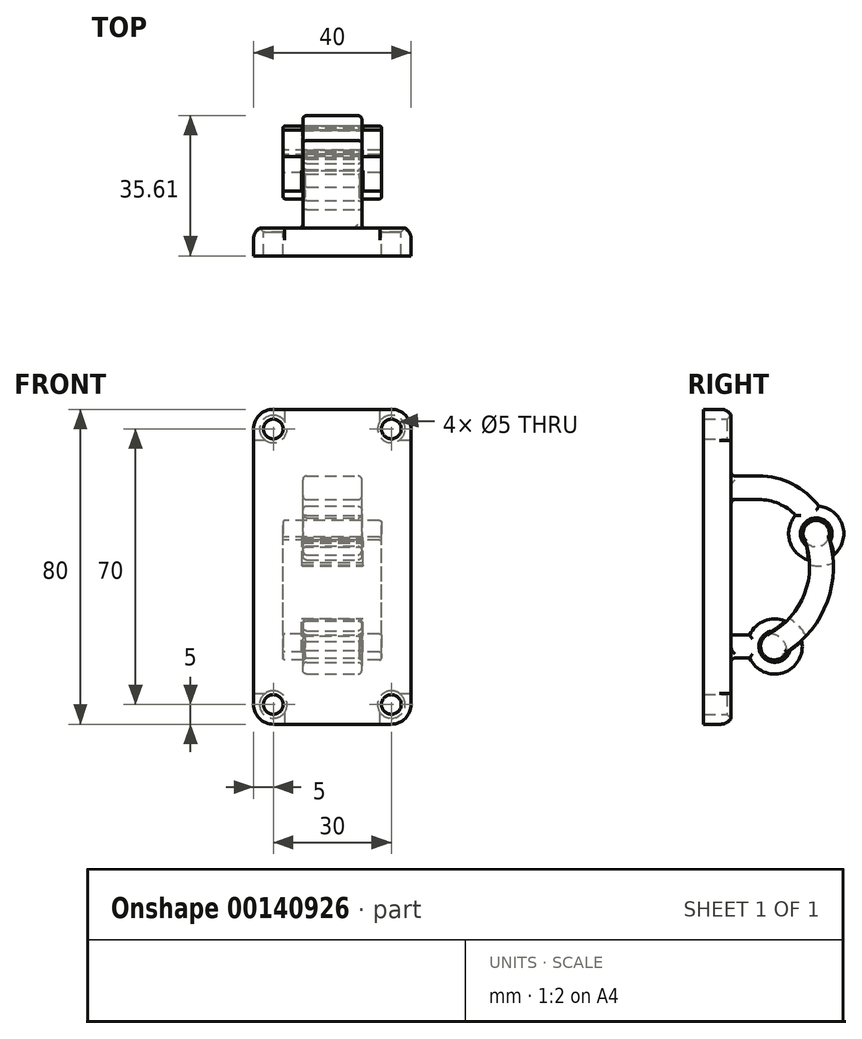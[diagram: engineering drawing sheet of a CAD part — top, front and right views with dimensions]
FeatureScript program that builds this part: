
annotation { "Feature Type Name" : "Feature", "Feature Type Description" : "" }
export const myFeature = defineFeature(function(context is Context, id is Id, definition is map)
    precondition{}
    {
        {
            var Q0;
            Q0=qCreatedBy(makeId("Front.planeOp"),FACE);
            var sketch = newSketch(context, id + "F0", { "sketchPlane" : qUnion([Q0])});
            skLineSegment(sketch, "E0.bottom", {"start": v(-15, 40) * mm, "end": v(15, 40) * mm});
            skLineSegment(sketch, "E0.top", {"start": v(-15, -40) * mm, "end": v(15, -40) * mm});
            skLineSegment(sketch, "E0.left", {"start": v(-20, 35) * mm, "end": v(-20, -35) * mm});
            skLineSegment(sketch, "E0.right", {"start": v(20, 35) * mm, "end": v(20, -35) * mm});
            skPoint(sketch, "E0.middle", {"position": v(0, 0) * mm});
            skLineSegment(sketch, "E1.bottom", {"start": v(-7.5, -17) * mm, "end": v(7.5, -17) * mm});
            skLineSegment(sketch, "E1.top", {"start": v(-7.5, -23) * mm, "end": v(7.5, -23) * mm});
            skLineSegment(sketch, "E1.left", {"start": v(-7.5, -17) * mm, "end": v(-7.5, -23) * mm});
            skLineSegment(sketch, "E1.right", {"start": v(7.5, -17) * mm, "end": v(7.5, -23) * mm});
            skPoint(sketch, "E1.middle", {"position": v(0, -20) * mm});
            skLineSegment(sketch, "E2.MirrorCS", {"start": v(-7.5, 17) * mm, "end": v(7.5, 17) * mm});
            skLineSegment(sketch, "E3.MirrorCS", {"start": v(-7.5, 17) * mm, "end": v(-7.5, 23) * mm});
            skLineSegment(sketch, "E4.MirrorCS", {"start": v(-7.5, 23) * mm, "end": v(7.5, 23) * mm});
            skLineSegment(sketch, "E5.MirrorCS", {"start": v(7.5, 17) * mm, "end": v(7.5, 23) * mm});
            skPoint(sketch, "E6.visualSharp", {"position": v(-20, 40) * mm});
            skArc(sketch, "E6.filletArc", {"start": v(-15, 40) * mm, "mid": v(-18.54, 38.54) * mm, "end": v(-20, 35) * mm});
            skPoint(sketch, "E7.visualSharp", {"position": v(20, 40) * mm});
            skArc(sketch, "E7.filletArc", {"start": v(20, 35) * mm, "mid": v(18.54, 38.54) * mm, "end": v(15, 40) * mm});
            skPoint(sketch, "E8.visualSharp", {"position": v(20, -40) * mm});
            skArc(sketch, "E8.filletArc", {"start": v(15, -40) * mm, "mid": v(18.54, -38.54) * mm, "end": v(20, -35) * mm});
            skPoint(sketch, "E9.visualSharp", {"position": v(-20, -40) * mm});
            skArc(sketch, "E9.filletArc", {"start": v(-20, -35) * mm, "mid": v(-18.54, -38.54) * mm, "end": v(-15, -40) * mm});
            skSolve(sketch);
        }
        {
            var Q0;
            Q0=makeQuery(id+"F0.imprint","IMPRINT",FACE,{"disambiguationData":[TD([[makeQuery(id+"F0.imprint","IMPRINT",EDGE,{"derivedFrom":sQuery(id+"F0.wireOp",EDGE,"E2.MirrorCS")}),1.0]])]});
            var Q1;
            Q1=makeQuery(id+"F0.imprint","IMPRINT",FACE,{"disambiguationData":[TD([[makeQuery(id+"F0.imprint","IMPRINT",EDGE,{"derivedFrom":sQuery(id+"F0.wireOp",EDGE,"E0.bottom")}),-1.0]])]});
            var Q2;
            Q2=makeQuery(id+"F0.imprint","IMPRINT",FACE,{"disambiguationData":[TD([[makeQuery(id+"F0.imprint","IMPRINT",EDGE,{"derivedFrom":sQuery(id+"F0.wireOp",EDGE,"E1.bottom")}),-1.0]])]});
            extrude(context, id + "F1", {"entities" : qUnion([Q0, Q1, Q2]), "oppositeDirection" : true, "depth" : 7 * mm});
        }
        {
            var Q0;
            Q0=qCreatedBy(makeId("Right.planeOp"),FACE);
            var sketch = newSketch(context, id + "F2", { "sketchPlane" : qUnion([Q0])});
            skLineSegment(sketch, "E10", {"start": v(-0.47, 23.07) * mm, "end": v(14, 23.07) * mm});
            skLineSegment(sketch, "E11", {"start": v(0, 17.07) * mm, "end": v(14, 17.07) * mm});
            skArc(sketch, "E12", {"start": v(14, 23.07) * mm, "mid": v(24.63, 19.8) * mm, "end": v(31.6, 11.16) * mm});
            skArc(sketch, "E13.0", {"start": v(14, 17.07) * mm, "mid": v(20.84, 15.11) * mm, "end": v(25.63, 9.84) * mm});
            skLineSegment(sketch, "E14", {"start": v(26.97, 4.3) * mm, "end": v(27.77, 4.32) * mm});
            skCircle(sketch, "E15", {"center": v(28.61, 8.4) * mm, "radius": 4 * mm});
            skLineSegment(sketch, "E16", {"start": v(0.13, -17.33) * mm, "end": v(11.71, -17.33) * mm});
            skLineSegment(sketch, "E17", {"start": v(0, -23.2) * mm, "end": v(11.71, -23.2) * mm});
            skArc(sketch, "E18", {"start": v(11.71, -23.2) * mm, "mid": v(25.07, -20.26) * mm, "end": v(11.71, -17.33) * mm});
            skCircle(sketch, "E19", {"center": v(18.07, -20.26) * mm, "radius": 4 * mm});
            skLineSegment(sketch, "E20.trimOffspring", {"start": v(18, -17.33) * mm, "end": v(18.13, -17.33) * mm});
            skLineSegment(sketch, "E21.trimOffspring", {"start": v(32.88, 4.4) * mm, "end": v(32.97, 4.4) * mm});
            skCircle(sketch, "E22.converted", {"center": v(28.61, 8.4) * mm, "radius": 7 * mm});
            skPoint(sketch, "E23.orphan", {"position": v(0, 23.07) * mm});
            skLineSegment(sketch, "E24", {"start": v(0, 23.07) * mm, "end": v(0, 17.07) * mm});
            skLineSegment(sketch, "E25", {"start": v(0.13, -17.33) * mm, "end": v(0, -23.2) * mm});
            skSolve(sketch);
        }
        {
            var Q0;
            Q0=makeQuery(id+"F1.opExtrude","CAP_FACE",FACE,{"disambiguationData":[OSD([sQuery(id+"F0.wireOp",EDGE,"E0.bottom"),sQuery(id+"F0.wireOp",EDGE,"E0.top"),sQuery(id+"F0.wireOp",EDGE,"E0.left"),sQuery(id+"F0.wireOp",EDGE,"E0.right"),sQuery(id+"F0.wireOp",EDGE,"E6.filletArc"),sQuery(id+"F0.wireOp",EDGE,"E7.filletArc"),sQuery(id+"F0.wireOp",EDGE,"E8.filletArc"),sQuery(id+"F0.wireOp",EDGE,"E9.filletArc")])],"isStart":false});
            var sketch = newSketch(context, id + "F3", { "sketchPlane" : qUnion([Q0])});
            skPoint(sketch, "E26", {"position": v(-15, 35) * mm});
            skPoint(sketch, "E27", {"position": v(15, 35) * mm});
            skPoint(sketch, "E28", {"position": v(15, -35) * mm});
            skPoint(sketch, "E29", {"position": v(-15, -35) * mm});
            skSolve(sketch);
        }
        {
            var Q0;
            Q0=sQuery(id+"F3.wireOp",VERTEX,"E27");
            var Q1;
            Q1=sQuery(id+"F3.wireOp",VERTEX,"E26");
            var Q2;
            Q2=sQuery(id+"F3.wireOp",VERTEX,"E28");
            var Q3;
            Q3=sQuery(id+"F3.wireOp",VERTEX,"E29");
            var Q4;
            Q4=makeQuery(id+"F1.opExtrude","SWEPT_BODY",BODY,{"disambiguationData":[OSD([sQuery(id+"F0.wireOp",EDGE,"E0.bottom"),sQuery(id+"F0.wireOp",EDGE,"E0.top"),sQuery(id+"F0.wireOp",EDGE,"E0.left"),sQuery(id+"F0.wireOp",EDGE,"E0.right"),sQuery(id+"F0.wireOp",EDGE,"E6.filletArc"),sQuery(id+"F0.wireOp",EDGE,"E7.filletArc"),sQuery(id+"F0.wireOp",EDGE,"E8.filletArc"),sQuery(id+"F0.wireOp",EDGE,"E9.filletArc")])]});
            hole(context, id + "F4", {"style" : HoleStyle.C_SINK, "endStyle" : HoleEndStyle.THROUGH, "holeDiameter" : 5 * mm, "cSinkDiameter" : 7 * mm, "cSinkAngle" : 90 * degree, "locations" : qUnion([Q0, Q1, Q2, Q3]), "scope" : qUnion([Q4]), "isTappedThrough" : true});
        }
        {
            var Q0;
            Q0=makeQuery(id+"F1.opExtrude","CAP_EDGE",EDGE,{"disambiguationData":[OSD([sQuery(id+"F0.wireOp",EDGE,"E0.bottom")])],"isStart":false});
            fillet(context, id + "F5", {"entities" : qUnion([Q0]), "radius" : 3 * mm, "tangentPropagation" : true, "allowEdgeOverflow" : false});
        }
        {
            var Q0;
            {var subQ1=sQuery(id+"F2.wireOp",EDGE,"E16");Q0=makeQuery(id+"F2.imprint","IMPRINT",FACE,{"disambiguationData":[TD([[makeQuery(id+"F2.imprint","IMPRINT",EDGE,{"derivedFrom":subQ1}),-1.0]])]});}
            var Q1;
            {var subQ0=sQuery(id+"F2.wireOp",EDGE,"C32lH3EJ-jwJ5-gCcF-TI2y-UIbqiRQANIjS");var subQ1=sQuery(id+"F2.wireOp",EDGE,"E18");var subQ2=makeQuery(id+"F2.imprint","INTERSECT",VERTEX,{"derivedFrom":[subQ1,subQ0]});Q1=makeQuery(id+"F2.imprint","IMPRINT",FACE,{"disambiguationData":[TD([[makeQuery(id+"F2.imprint","IMPRINT",EDGE,{"disambiguationData":[TD([[subQ2,-1.0]])],"derivedFrom":subQ1}),1.0]])]});}
            var Q2;
            Q2=makeQuery(id+"F2.imprint","IMPRINT",FACE,{"disambiguationData":[TD([[makeQuery(id+"F2.imprint","IMPRINT",EDGE,{"derivedFrom":sQuery(id+"F2.wireOp",EDGE,"E11")}),1.0]])]});
            var Q3;
            {var subQ3=sQuery(id+"F2.wireOp",EDGE,"E15");var subQ7=sQuery(id+"F2.wireOp",EDGE,"lnQvz7nI-boOK-pGjN-hhzM-7sdql3FDUyVG");var subQ9=makeQuery(id+"F2.imprint","INTERSECT",VERTEX,{"derivedFrom":[subQ3,subQ7]});Q3=makeQuery(id+"F2.imprint","IMPRINT",FACE,{"disambiguationData":[TD([[makeQuery(id+"F2.imprint","IMPRINT",EDGE,{"disambiguationData":[TD([[subQ9,1.0]])],"derivedFrom":subQ3}),-1.0]])]});}
            var Q4;
            {var subQ0=sQuery(id+"F2.wireOp",EDGE,"lnQvz7nI-boOK-pGjN-hhzM-7sdql3FDUyVG");var subQ1=sQuery(id+"F2.wireOp",EDGE,"E15");var subQ2=makeQuery(id+"F2.imprint","INTERSECT",VERTEX,{"derivedFrom":[subQ1,subQ0]});Q4=makeQuery(id+"F2.imprint","IMPRINT",FACE,{"disambiguationData":[TD([[makeQuery(id+"F2.imprint","IMPRINT",EDGE,{"disambiguationData":[TD([[subQ2,-1.0]])],"derivedFrom":subQ1}),-1.0]])]});}
            var Q5;
            Q5=makeQuery(id+"F2.imprint","IMPRINT",FACE,{"disambiguationData":[TD([[makeQuery(id+"F2.imprint","IMPRINT",EDGE,{"derivedFrom":sQuery(id+"F2.wireOp",EDGE,"E15")}),-1.0]])]});
            extrude(context, id + "F6", {"entities" : qUnion([Q0, Q1, Q2, Q3, Q4, Q5]), "operationType" : NewBodyOperationType.ADD, "endBound" : BoundingType.SYMMETRIC, "oppositeDirection" : true, "depth" : 15 * mm});
        }
        {
            var Q0;
            Q0=qCreatedBy(makeId("Right.planeOp"),FACE);
            var sketch = newSketch(context, id + "F7", { "sketchPlane" : qUnion([Q0])});
            skCircle(sketch, "E30", {"center": v(28.62, 8.41) * mm, "radius": 3.35 * mm});
            skCircle(sketch, "E31", {"center": v(17.95, -20.2) * mm, "radius": 3.47 * mm});
            skPoint(sketch, "E31.first.point", {"position": v(20.72, -22.3) * mm});
            skPoint(sketch, "E31.second.point", {"position": v(17.62, -16.74) * mm});
            skPoint(sketch, "E31.third.point", {"position": v(16.3, -23.25) * mm});
            skArc(sketch, "E32", {"start": v(16.5, -17.04) * mm, "mid": v(25.78, -6.5) * mm, "end": v(25.39, 7.52) * mm});
            skArc(sketch, "E33", {"start": v(21.11, -21.64) * mm, "mid": v(31.41, -8.88) * mm, "end": v(31.84, 7.52) * mm});
            skSolve(sketch);
        }
        {
            var Q0;
            Q0 = qSketchRegion(id + "F7", true);
            extrude(context, id + "F8", {"entities" : qUnion([Q0]), "endBound" : BoundingType.SYMMETRIC, "depth" : 25 * mm});
        }
        {
            var Q0;
            Q0=qCreatedBy(makeId("Right.planeOp"),FACE);
            var sketch = newSketch(context, id + "F9", { "sketchPlane" : qUnion([Q0])});
            skArc(sketch, "E34", {"start": v(25.8, 6.56) * mm, "mid": v(29.05, 5.1) * mm, "end": v(31.79, 7.38) * mm});
            skPoint(sketch, "E34.first.point", {"position": v(26.92, 11.33) * mm});
            skPoint(sketch, "E34.second.point", {"position": v(31.94, 8.18) * mm});
            skPoint(sketch, "E34.third.point", {"position": v(25.3, 7.76) * mm});
            skArc(sketch, "E35", {"start": v(26.54, 0.56) * mm, "mid": v(26.42, 3.6) * mm, "end": v(25.8, 6.56) * mm});
            skArc(sketch, "E36", {"start": v(33.14, 1.12) * mm, "mid": v(32.9, 4.34) * mm, "end": v(31.79, 7.38) * mm});
            skArc(sketch, "E37", {"start": v(26.54, 0.56) * mm, "mid": v(29.89, 0.24) * mm, "end": v(33.14, 1.12) * mm});
            skSolve(sketch);
        }
        {
            var Q0;
            Q0 = qSketchRegion(id + "F9", true);
            extrude(context, id + "F10", {"entities" : qUnion([Q0]), "operationType" : NewBodyOperationType.REMOVE, "endBound" : BoundingType.SYMMETRIC, "oppositeDirection" : true, "depth" : 15.5 * mm});
        }
        {
            var Q0;
            Q0=qCreatedBy(makeId("Right.planeOp"),FACE);
            var sketch = newSketch(context, id + "F11", { "sketchPlane" : qUnion([Q0])});
            skArc(sketch, "E38", {"start": v(26.12, -17.83) * mm, "mid": v(24.18, -15.06) * mm, "end": v(21.44, -13.08) * mm});
            skPoint(sketch, "E39.first.point", {"position": v(15.16, -17.97) * mm});
            skPoint(sketch, "E39.second.point", {"position": v(15.34, -22.6) * mm});
            skPoint(sketch, "E39.third.point", {"position": v(18.5, -23.71) * mm});
            skArc(sketch, "E40", {"start": v(16.28, -17.02) * mm, "mid": v(18.99, -15.22) * mm, "end": v(21.44, -13.08) * mm});
            skArc(sketch, "E41", {"start": v(21.13, -21.86) * mm, "mid": v(23.73, -19.97) * mm, "end": v(26.12, -17.83) * mm});
            skArc(sketch, "E42", {"start": v(21.13, -21.86) * mm, "mid": v(19.84, -18.3) * mm, "end": v(16.28, -17.02) * mm});
            skSolve(sketch);
        }
        {
            var Q0;
            Q0 = qSketchRegion(id + "F11", true);
            extrude(context, id + "F12", {"entities" : qUnion([Q0]), "operationType" : NewBodyOperationType.REMOVE, "endBound" : BoundingType.SYMMETRIC, "oppositeDirection" : true, "depth" : 15.6 * mm});
        }
        {
            var Q0;
            Q0=qCreatedBy(makeId("Right.planeOp"),FACE);
            var sketch = newSketch(context, id + "F13", { "sketchPlane" : qUnion([Q0])});
            skCircle(sketch, "E43", {"center": v(17.97, -20.18) * mm, "radius": 3.57 * mm});
            skPoint(sketch, "E43.first.point", {"position": v(15.52, -17.58) * mm});
            skPoint(sketch, "E43.second.point", {"position": v(15.23, -22.48) * mm});
            skPoint(sketch, "E43.third.point", {"position": v(17.86, -23.75) * mm});
            skSolve(sketch);
        }
        {
            var Q0;
            Q0 = qSketchRegion(id + "F13", true);
            extrude(context, id + "F14", {"entities" : qUnion([Q0]), "operationType" : NewBodyOperationType.REMOVE, "endBound" : BoundingType.SYMMETRIC, "oppositeDirection" : true, "depth" : 13.8 * mm});
        }
        {
            var Q0;
            Q0=makeQuery(id+"F6.opExtrude","CAP_EDGE",EDGE,{"disambiguationData":[OSD([sQuery(id+"F2.wireOp",EDGE,"E16")])],"isStart":true});
            var Q1;
            Q1=makeQuery(id+"F6.opExtrude","CAP_EDGE",EDGE,{"disambiguationData":[OSD([sQuery(id+"F2.wireOp",EDGE,"E18")])],"isStart":true});
            var Q2;
            Q2=makeQuery(id+"F6.opExtrude","CAP_EDGE",EDGE,{"disambiguationData":[OSD([sQuery(id+"F2.wireOp",EDGE,"E17")])],"isStart":true});
            var Q3;
            Q3=makeQuery(id+"F6.opExtrude","CAP_EDGE",EDGE,{"disambiguationData":[OSD([sQuery(id+"F2.wireOp",EDGE,"E19")])],"isStart":true});
            var Q4;
            Q4=makeQuery(id+"F6.opExtrude","CAP_EDGE",EDGE,{"disambiguationData":[OSD([sQuery(id+"F2.wireOp",EDGE,"E22.converted")])],"isStart":true});
            var Q5;
            Q5=makeQuery(id+"F6.opExtrude","CAP_EDGE",EDGE,{"disambiguationData":[OSD([sQuery(id+"F2.wireOp",EDGE,"E15")])],"isStart":true});
            var Q6;
            Q6=makeQuery(id+"F6.opExtrude","CAP_EDGE",EDGE,{"disambiguationData":[OSD([sQuery(id+"F2.wireOp",EDGE,"E13.0")])],"isStart":true});
            var Q7;
            Q7=makeQuery(id+"F6.opExtrude","CAP_EDGE",EDGE,{"disambiguationData":[OSD([sQuery(id+"F2.wireOp",EDGE,"E11")])],"isStart":true});
            var Q8;
            Q8=makeQuery(id+"F6.opExtrude","CAP_EDGE",EDGE,{"disambiguationData":[OSD([sQuery(id+"F2.wireOp",EDGE,"E12")])],"isStart":true});
            var Q9;
            Q9=makeQuery(id+"F6.opExtrude","CAP_EDGE",EDGE,{"disambiguationData":[OSD([sQuery(id+"F2.wireOp",EDGE,"E10")])],"isStart":true});
            var Q10;
            Q10=makeQuery(id+"F6.opExtrude","CAP_EDGE",EDGE,{"disambiguationData":[OSD([sQuery(id+"F2.wireOp",EDGE,"E12")])],"isStart":false});
            var Q11;
            Q11=makeQuery(id+"F6.opExtrude","CAP_EDGE",EDGE,{"disambiguationData":[OSD([sQuery(id+"F2.wireOp",EDGE,"E22.converted")])],"isStart":false});
            var Q12;
            Q12=makeQuery(id+"F6.opExtrude","CAP_EDGE",EDGE,{"disambiguationData":[OSD([sQuery(id+"F2.wireOp",EDGE,"E13.0")])],"isStart":false});
            var Q13;
            Q13=makeQuery(id+"F6.opExtrude","CAP_EDGE",EDGE,{"disambiguationData":[OSD([sQuery(id+"F2.wireOp",EDGE,"E15")])],"isStart":false});
            var Q14;
            Q14=makeQuery(id+"F6.opExtrude","CAP_EDGE",EDGE,{"disambiguationData":[OSD([sQuery(id+"F2.wireOp",EDGE,"E16")])],"isStart":false});
            var Q15;
            Q15=makeQuery(id+"F6.opExtrude","CAP_EDGE",EDGE,{"disambiguationData":[OSD([sQuery(id+"F2.wireOp",EDGE,"E18")])],"isStart":false});
            var Q16;
            Q16=makeQuery(id+"F6.opExtrude","CAP_EDGE",EDGE,{"disambiguationData":[OSD([sQuery(id+"F2.wireOp",EDGE,"E19")])],"isStart":false});
            var Q17;
            Q17=makeQuery(id+"F6.opExtrude","CAP_EDGE",EDGE,{"disambiguationData":[OSD([sQuery(id+"F2.wireOp",EDGE,"E17")])],"isStart":false});
            var Q18;
            Q18=makeQuery(id+"F6.boolean.opBoolean","INTERSECT",EDGE,{"derivedFrom":[makeQuery(id+"F1.opExtrude","CAP_FACE",FACE,{"disambiguationData":[OSD([sQuery(id+"F0.wireOp",EDGE,"E0.bottom"),sQuery(id+"F0.wireOp",EDGE,"E0.top"),sQuery(id+"F0.wireOp",EDGE,"E0.left"),sQuery(id+"F0.wireOp",EDGE,"E0.right"),sQuery(id+"F0.wireOp",EDGE,"E6.filletArc"),sQuery(id+"F0.wireOp",EDGE,"E7.filletArc"),sQuery(id+"F0.wireOp",EDGE,"E8.filletArc"),sQuery(id+"F0.wireOp",EDGE,"E9.filletArc")])],"isStart":false}),makeQuery(id+"F6.opExtrude","SWEPT_FACE",FACE,{"disambiguationData":[OSD([sQuery(id+"F2.wireOp",EDGE,"E17")])]})]});
            var Q19;
            Q19=makeQuery(id+"F6.boolean.opBoolean","INTERSECT",EDGE,{"derivedFrom":[makeQuery(id+"F1.opExtrude","CAP_FACE",FACE,{"disambiguationData":[OSD([sQuery(id+"F0.wireOp",EDGE,"E0.bottom"),sQuery(id+"F0.wireOp",EDGE,"E0.top"),sQuery(id+"F0.wireOp",EDGE,"E0.left"),sQuery(id+"F0.wireOp",EDGE,"E0.right"),sQuery(id+"F0.wireOp",EDGE,"E6.filletArc"),sQuery(id+"F0.wireOp",EDGE,"E7.filletArc"),sQuery(id+"F0.wireOp",EDGE,"E8.filletArc"),sQuery(id+"F0.wireOp",EDGE,"E9.filletArc")])],"isStart":false}),makeQuery(id+"F6.opExtrude","CAP_FACE",FACE,{"disambiguationData":[OSD([sQuery(id+"F2.wireOp",EDGE,"E10"),sQuery(id+"F2.wireOp",EDGE,"E11"),sQuery(id+"F2.wireOp",EDGE,"E12"),sQuery(id+"F2.wireOp",EDGE,"E13.0"),sQuery(id+"F2.wireOp",EDGE,"E15"),sQuery(id+"F2.wireOp",EDGE,"E22.converted"),sQuery(id+"F2.wireOp",EDGE,"E24")])],"isStart":true})]});
            var Q20;
            Q20=makeQuery(id+"F6.boolean.opBoolean","INTERSECT",EDGE,{"derivedFrom":[makeQuery(id+"F1.opExtrude","CAP_FACE",FACE,{"disambiguationData":[OSD([sQuery(id+"F0.wireOp",EDGE,"E0.bottom"),sQuery(id+"F0.wireOp",EDGE,"E0.top"),sQuery(id+"F0.wireOp",EDGE,"E0.left"),sQuery(id+"F0.wireOp",EDGE,"E0.right"),sQuery(id+"F0.wireOp",EDGE,"E6.filletArc"),sQuery(id+"F0.wireOp",EDGE,"E7.filletArc"),sQuery(id+"F0.wireOp",EDGE,"E8.filletArc"),sQuery(id+"F0.wireOp",EDGE,"E9.filletArc")])],"isStart":false}),makeQuery(id+"F6.opExtrude","SWEPT_FACE",FACE,{"disambiguationData":[OSD([sQuery(id+"F2.wireOp",EDGE,"E10")])]})]});
            var Q21;
            Q21=makeQuery(id+"F6.opExtrude","CAP_EDGE",EDGE,{"disambiguationData":[OSD([sQuery(id+"F2.wireOp",EDGE,"E10")])],"isStart":false});
            fillet(context, id + "F15", {"entities" : qUnion([Q0, Q1, Q2, Q3, Q4, Q5, Q6, Q7, Q8, Q9, Q10, Q11, Q12, Q13, Q14, Q15, Q16, Q17, Q18, Q19, Q20, Q21]), "radius" : 1 * mm, "tangentPropagation" : true, "allowEdgeOverflow" : false});
        }
        {
            var Q0;
            Q0=makeQuery(id+"F8.opExtrude","CAP_EDGE",EDGE,{"disambiguationData":[OSD([sQuery(id+"F7.wireOp",EDGE,"E32")])],"isStart":false});
            var Q1;
            Q1=makeQuery(id+"F8.opExtrude","CAP_EDGE",EDGE,{"disambiguationData":[OSD([sQuery(id+"F7.wireOp",EDGE,"E33")])],"isStart":false});
            var Q2;
            Q2=makeQuery(id+"F8.opExtrude","CAP_EDGE",EDGE,{"disambiguationData":[OSD([sQuery(id+"F7.wireOp",EDGE,"E30")])],"isStart":false});
            var Q3;
            Q3=makeQuery(id+"F8.opExtrude","CAP_EDGE",EDGE,{"disambiguationData":[OSD([sQuery(id+"F7.wireOp",EDGE,"E31")])],"isStart":false});
            var Q4;
            Q4=makeQuery(id+"F8.opExtrude","CAP_EDGE",EDGE,{"disambiguationData":[OSD([sQuery(id+"F7.wireOp",EDGE,"E32")])],"isStart":true});
            var Q5;
            Q5=makeQuery(id+"F8.opExtrude","CAP_EDGE",EDGE,{"disambiguationData":[OSD([sQuery(id+"F7.wireOp",EDGE,"E33")])],"isStart":true});
            var Q6;
            Q6=makeQuery(id+"F8.opExtrude","CAP_EDGE",EDGE,{"disambiguationData":[OSD([sQuery(id+"F7.wireOp",EDGE,"E31")])],"isStart":true});
            var Q7;
            Q7=makeQuery(id+"F8.opExtrude","CAP_EDGE",EDGE,{"disambiguationData":[OSD([sQuery(id+"F7.wireOp",EDGE,"E30")])],"isStart":true});
            fillet(context, id + "F16", {"entities" : qUnion([Q0, Q1, Q2, Q3, Q4, Q5, Q6, Q7]), "radius" : .5 * mm, "tangentPropagation" : true, "allowEdgeOverflow" : false});
        }
        {
            var Q0;
            Q0=makeQuery(id+"F14.boolean.opBoolean","INTERSECT",EDGE,{"derivedFrom":[makeQuery(id+"F8.opExtrude","SWEPT_FACE",FACE,{"disambiguationData":[OSD([sQuery(id+"F7.wireOp",EDGE,"E31")])]}),makeQuery(id+"F14.opExtrude","CAP_FACE",FACE,{"disambiguationData":[OSD([sQuery(id+"F13.wireOp",EDGE,"E43")])],"isStart":false})]});
            var Q1;
            Q1=makeQuery(id+"F14.boolean.opBoolean","INTERSECT",EDGE,{"derivedFrom":[makeQuery(id+"F8.opExtrude","SWEPT_FACE",FACE,{"disambiguationData":[OSD([sQuery(id+"F7.wireOp",EDGE,"E31")])]}),makeQuery(id+"F14.opExtrude","CAP_FACE",FACE,{"disambiguationData":[OSD([sQuery(id+"F13.wireOp",EDGE,"E43")])],"isStart":true})]});
            fillet(context, id + "F17", {"entities" : qUnion([Q0, Q1]), "radius" : .5 * mm, "tangentPropagation" : true, "allowEdgeOverflow" : false});
        }
        {
            var Q0;
            Q0=makeQuery(id+"F14.boolean.opBoolean","INTERSECT",EDGE,{"derivedFrom":[makeQuery(id+"F12.boolean.opBoolean","COPY",FACE,{"derivedFrom":makeQuery(id+"F12.opExtrude","SWEPT_FACE",FACE,{"disambiguationData":[OSD([sQuery(id+"F11.wireOp",EDGE,"E42")])]})}),makeQuery(id+"F14.opExtrude","CAP_FACE",FACE,{"disambiguationData":[OSD([sQuery(id+"F13.wireOp",EDGE,"E43")])],"isStart":false})]});
            var Q1;
            Q1=makeQuery(id+"F14.boolean.opBoolean","INTERSECT",EDGE,{"derivedFrom":[makeQuery(id+"F12.boolean.opBoolean","COPY",FACE,{"derivedFrom":makeQuery(id+"F12.opExtrude","SWEPT_FACE",FACE,{"disambiguationData":[OSD([sQuery(id+"F11.wireOp",EDGE,"E42")])]})}),makeQuery(id+"F14.opExtrude","CAP_FACE",FACE,{"disambiguationData":[OSD([sQuery(id+"F13.wireOp",EDGE,"E43")])],"isStart":true})]});
            fillet(context, id + "F18", {"entities" : qUnion([Q0, Q1]), "radius" : .5 * mm, "tangentPropagation" : true, "allowEdgeOverflow" : false});
        }
    });
